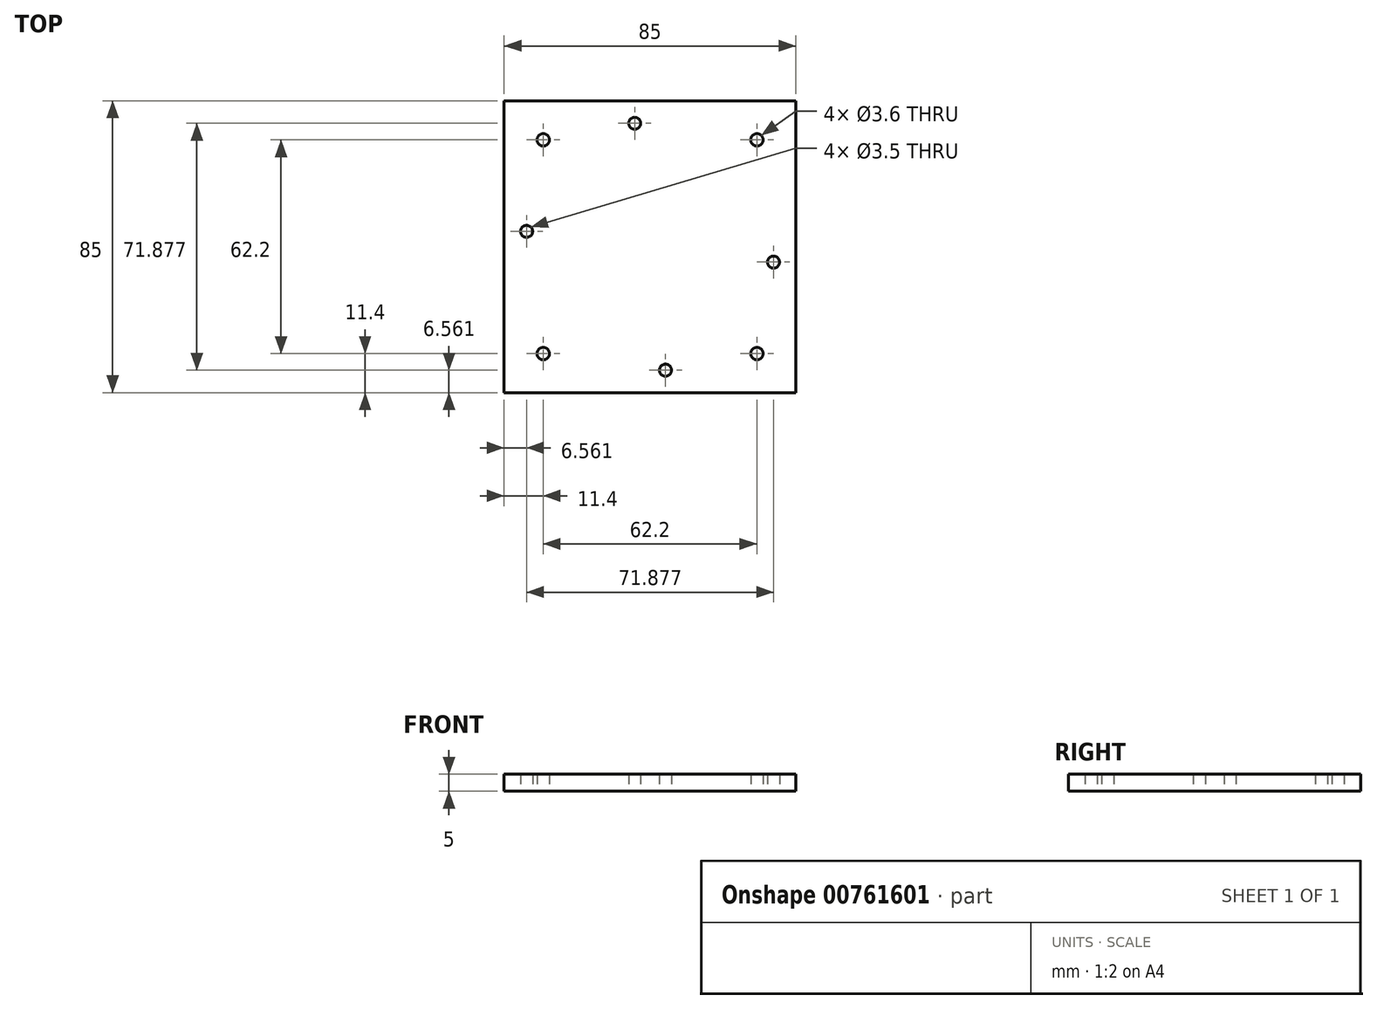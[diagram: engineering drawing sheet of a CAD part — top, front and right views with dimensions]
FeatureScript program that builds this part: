
annotation { "Feature Type Name" : "Feature", "Feature Type Description" : "" }
export const myFeature = defineFeature(function(context is Context, id is Id, definition is map)
    precondition{}
    {
        {
            var Q0;
            Q0=qCreatedBy(makeId("Top.planeOp"),FACE);
            var sketch = newSketch(context, id + "F0", { "sketchPlane" : qUnion([Q0])});
            skLineSegment(sketch, "E0.bottom", {"start": v(42.5, -42.5) * mm, "end": v(-42.5, -42.5) * mm});
            skLineSegment(sketch, "E0.top", {"start": v(42.5, 42.5) * mm, "end": v(-42.5, 42.5) * mm});
            skLineSegment(sketch, "E0.left", {"start": v(42.5, -42.5) * mm, "end": v(42.5, 42.5) * mm});
            skLineSegment(sketch, "E0.right", {"start": v(-42.5, -42.5) * mm, "end": v(-42.5, 42.5) * mm});
            skPoint(sketch, "E0.middle", {"position": v(0, 0) * mm});
            skLineSegment(sketch, "E1.bottom", {"start": v(31.1, -31.1) * mm, "end": v(-31.1, -31.1) * mm, "construction": true});
            skLineSegment(sketch, "E1.top", {"start": v(31.1, 31.1) * mm, "end": v(-31.1, 31.1) * mm, "construction": true});
            skLineSegment(sketch, "E1.left", {"start": v(31.1, -31.1) * mm, "end": v(31.1, 31.1) * mm, "construction": true});
            skLineSegment(sketch, "E1.right", {"start": v(-31.1, -31.1) * mm, "end": v(-31.1, 31.1) * mm, "construction": true});
            skCircle(sketch, "E2", {"center": v(-31.1, 31.1) * mm, "radius": 1.8 * mm});
            skCircle(sketch, "E3.MirrorC", {"center": v(31.1, 31.1) * mm, "radius": 1.8 * mm});
            skCircle(sketch, "E4.MirrorC", {"center": v(-31.1, -31.1) * mm, "radius": 1.8 * mm});
            skCircle(sketch, "E5.MirrorC", {"center": v(31.1, -31.1) * mm, "radius": 1.8 * mm});
            skSolve(sketch);
        }
        {
            var Q0;
            Q0=makeQuery(id+"F0.imprint","IMPRINT",FACE,{"disambiguationData":[TD([[makeQuery(id+"F0.imprint","IMPRINT",EDGE,{"derivedFrom":sQuery(id+"F0.wireOp",EDGE,"E0.bottom")}),-1.0]])]});
            var sketch = newSketch(context, id + "F1", { "sketchPlane" : qUnion([Q0])});
            skPoint(sketch, "E6.middle", {"position": v(0, 0) * mm});
            skLineSegment(sketch, "E7", {"start": v(-4.47, 35.94) * mm, "end": v(-35.94, 4.47) * mm, "construction": true});
            skLineSegment(sketch, "E8", {"start": v(-35.94, 4.47) * mm, "end": v(4.47, -35.94) * mm, "construction": true});
            skLineSegment(sketch, "E9", {"start": v(-4.47, 35.94) * mm, "end": v(35.94, -4.47) * mm, "construction": true});
            skLineSegment(sketch, "E10", {"start": v(35.94, -4.47) * mm, "end": v(4.47, -35.94) * mm, "construction": true});
            skCircle(sketch, "E11", {"center": v(-4.47, 35.94) * mm, "radius": 1.75 * mm});
            skCircle(sketch, "E12", {"center": v(35.94, -4.47) * mm, "radius": 1.75 * mm});
            skCircle(sketch, "E13", {"center": v(4.47, -35.94) * mm, "radius": 1.75 * mm});
            skCircle(sketch, "E14", {"center": v(-35.94, 4.47) * mm, "radius": 1.75 * mm});
            skLineSegment(sketch, "E15.bottom", {"start": v(42.5, -42.5) * mm, "end": v(-42.5, -42.5) * mm, "construction": true});
            skLineSegment(sketch, "E15.top", {"start": v(42.5, 42.5) * mm, "end": v(-42.5, 42.5) * mm, "construction": true});
            skLineSegment(sketch, "E15.left", {"start": v(42.5, -42.5) * mm, "end": v(42.5, 42.5) * mm, "construction": true});
            skLineSegment(sketch, "E15.right", {"start": v(-42.5, -42.5) * mm, "end": v(-42.5, 42.5) * mm, "construction": true});
            skSolve(sketch);
        }
        {
            var Q0;
            Q0 = qSketchRegion(id + "F0", true);
            var Q1;
            Q1=qCreatedBy(makeId("Right.planeOp"),FACE);
            extrude(context, id + "F2", {"entities" : qUnion([Q0]), "depth" : 5 * mm, "endBoundEntityFace" : qUnion([Q1]), "offsetDistance" : 25 * mm});
        }
        {
            var Q0;
            Q0 = qSketchRegion(id + "F1", true);
            extrude(context, id + "F3", {"entities" : qUnion([Q0]), "operationType" : NewBodyOperationType.REMOVE, "depth" : 10 * mm, "offsetDistance" : 25 * mm});
        }
    });
